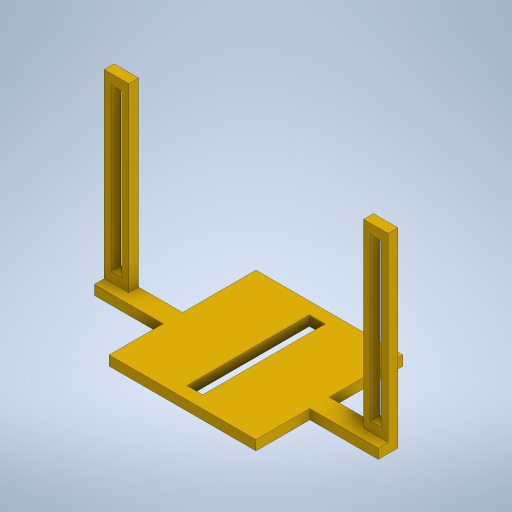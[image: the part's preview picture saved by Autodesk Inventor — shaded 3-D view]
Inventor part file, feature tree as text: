
AUTODESK INVENTOR PART (.ipt)
format: ipt  version: 2024 (Build 280153000, 153)  size: 342,528 bytes
history: native  units: in
note: dims shown in document units (in); Inventor stores cm internally (conversion verified against a paired STEP export)
features: extrude x6, sketch x1
ambient origin geometry x8: Origin, YZ Plane, XZ Plane, XY Plane, X Axis, Y Axis, Z Axis, Center Point
bodies: Body1 (feature_tree)
feature tree (7):
  extrude  "Extrusion2"  Depth=1.1811in
  extrude  "Extrusion5"  Depth=0.0787in TaperAngle=0.0deg
  extrude  "Extrusion6"  Depth=0.9843in
  extrude  "Extrusion7"  TaperAngle=0.0deg  [1 undecoded]
  extrude  "Extrusion8"  Depth=0.126in
  extrude  "Extrusion9"  Depth=0.0984in
  sketch  "Sketch2"  dims[d0=1.1811in d1=1.1811in d6=0.0787in d7=0.0in d21=0.9843in d22=0.0in d23=0.0in d25=0.126in d26=0.0984in d28=0.5906in d29=0.1575in d30=0.0787in d31=0.5512in d32=0.0in d33=0.5906in d34=0.1575in d35=0.5512in d36=0.0in d37=0.1969in d38=0.0787in d39=0.1969in d40=0.0787in d41=1.4567in d42=0.0in d43=0.0787in d44=0.0787in d45=0.0551in d46=0.0551in d47=0.0866in d50=0.0551in d51=0.0551in d52=0.0787in d53=0.0787in d54=0.5512in d55=0.0in d56=0.5906in]
note: 1 required parameter value undecoded (feature->parameter linkage not recoverable at this tier; creation-order binding heuristic only, values carry confidence <= 0.55)
